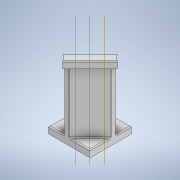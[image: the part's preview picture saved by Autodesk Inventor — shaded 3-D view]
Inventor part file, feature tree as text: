
AUTODESK INVENTOR PART (.ipt)
format: ipt  version: 2022 (Build 260153000, 153)  size: 217,088 bytes
history: native  units: in
note: dims shown in document units (in); Inventor stores cm internally (conversion verified against a paired STEP export)
features: extrude x5, sketch x5, plane x3, fillet x1
ambient origin geometry x8: Origin, YZ Plane, XZ Plane, XY Plane, X Axis, Y Axis, Z Axis, Center Point
bodies: Solid1 (feature_tree)
feature tree (14):
  extrude  "Extrusion1"  Depth=1.1811in
  extrude  "Extrusion2"  Depth=0.1969in TaperAngle=0.0deg
  plane  "Work Plane1"
  plane  "Work Plane2"
  plane  "Work Plane3"
  sketch  "Sketch3"  dims[d5=1.9685in d6=0.0in d7=0.2953in d8=-0.2953in]
  sketch  "Sketch4"  dims[d15=0.0787in d16=0.0in d17=0.0787in d18=0.0in]
  extrude  "Extrusion3"  Depth=0.2953in
  extrude  "Extrusion4"  Depth=0.0787in TaperAngle=0.0deg
  extrude  "Extrusion5"  Depth=0.2362in TaperAngle=0.0deg
  fillet  "Fillet1"  Radius=0.0295in
  sketch  "Sketch1"  dims[d0=1.1811in d1=1.1811in]
  sketch  "Sketch2"  dims[d2=0.1575in d3=0.1969in d4=0.0in]
  sketch  "Sketch5"  dims[d19=0.1969in d20=0.2362in d21=0.0in d22=0.0295in]
